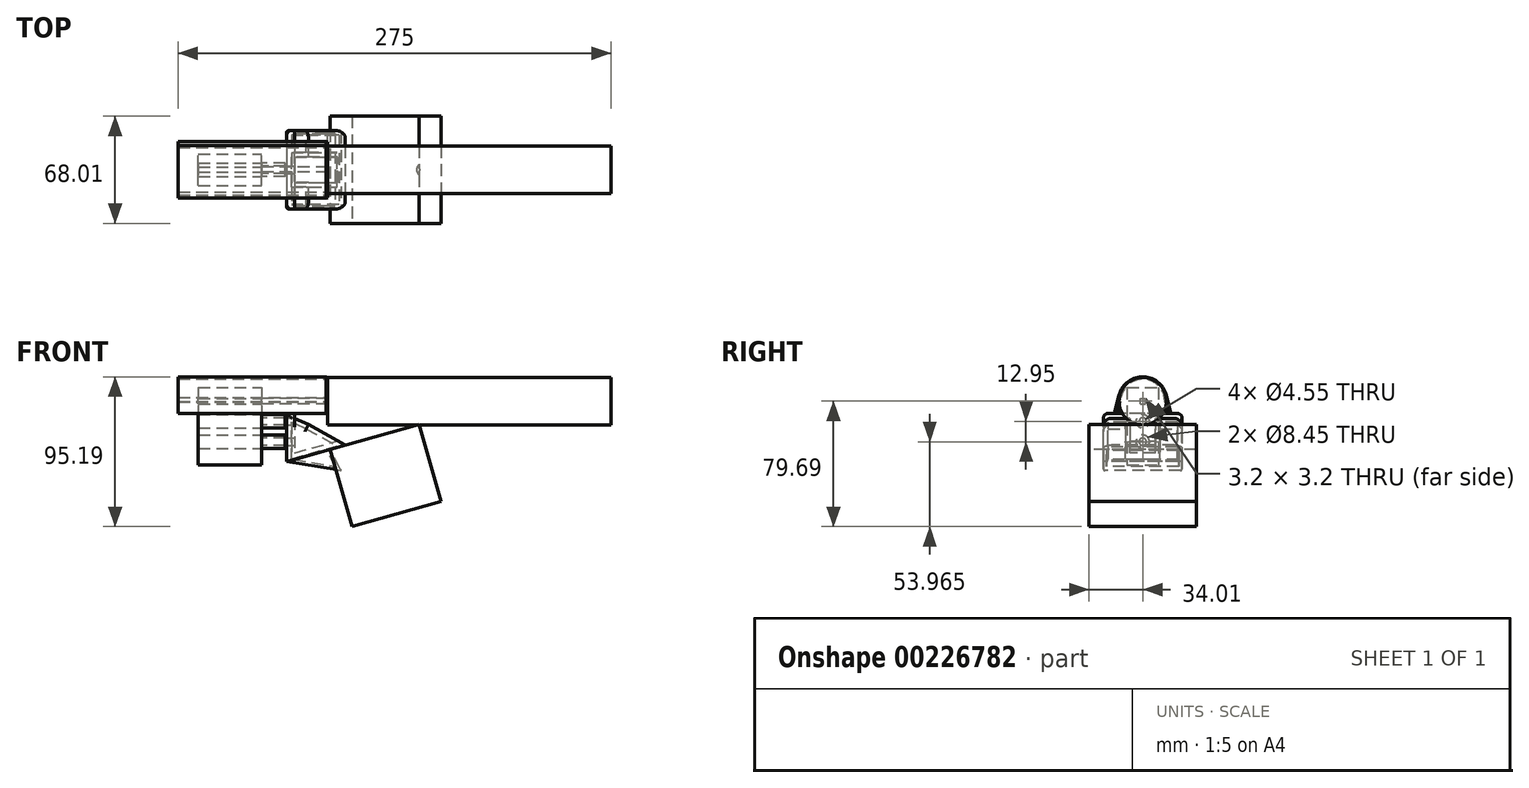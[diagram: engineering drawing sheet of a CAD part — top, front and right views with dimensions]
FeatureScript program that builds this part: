
annotation { "Feature Type Name" : "Feature", "Feature Type Description" : "" }
export const myFeature = defineFeature(function(context is Context, id is Id, definition is map)
    precondition{}
    {
        {
            var Q0;
            Q0=qCreatedBy(makeId("Right.planeOp"),FACE);
            var sketch = newSketch(context, id + "F0", { "sketchPlane" : qUnion([Q0])});
            skLineSegment(sketch, "E0.bottom", {"start": v(-20, 49.25) * mm, "end": v(0, 49.25) * mm});
            skLineSegment(sketch, "E0.top", {"start": v(-20, 0) * mm, "end": v(0, 0) * mm});
            skLineSegment(sketch, "E0.left", {"start": v(-20, 49.25) * mm, "end": v(-20, 0) * mm});
            skLineSegment(sketch, "E0.right", {"start": v(0, 49.25) * mm, "end": v(0, 0) * mm});
            skLineSegment(sketch, "E1.bottom", {"start": v(-11.6, 38.98) * mm, "end": v(-8.4, 38.98) * mm});
            skLineSegment(sketch, "E1.top", {"start": v(-11.6, 42.18) * mm, "end": v(-8.4, 42.18) * mm});
            skLineSegment(sketch, "E1.left", {"start": v(-11.6, 38.98) * mm, "end": v(-11.6, 42.18) * mm});
            skLineSegment(sketch, "E1.right", {"start": v(-8.4, 38.98) * mm, "end": v(-8.4, 42.18) * mm});
            skCircle(sketch, "E2", {"center": v(-10, 27.8) * mm, "radius": 4.22 * mm});
            skCircle(sketch, "E3", {"center": v(-10, 14.86) * mm, "radius": 4.22 * mm});
            skPoint(sketch, "E4", {"position": v(-10, 0) * mm});
            skPoint(sketch, "E5", {"position": v(-10, 38.98) * mm});
            skCircle(sketch, "E6", {"center": v(-10, 27.8) * mm, "radius": 2.27 * mm});
            skCircle(sketch, "E7", {"center": v(-10, 14.86) * mm, "radius": 2.27 * mm});
            skSolve(sketch);
        }
        {
            var Q0;
            Q0=makeQuery(id+"F0.imprint","IMPRINT",FACE,{"disambiguationData":[TD([[makeQuery(id+"F0.imprint","IMPRINT",EDGE,{"derivedFrom":sQuery(id+"F0.wireOp",EDGE,"E2")}),1.0]])]});
            var Q1;
            Q1=makeQuery(id+"F0.imprint","IMPRINT",FACE,{"disambiguationData":[TD([[makeQuery(id+"F0.imprint","IMPRINT",EDGE,{"derivedFrom":sQuery(id+"F0.wireOp",EDGE,"E3")}),1.0]])]});
            extrude(context, id + "F1", {"entities" : qUnion([Q0, Q1]), "depth" : 15 * mm});
        }
        {
            var Q0;
            Q0=makeQuery(id+"F0.imprint","IMPRINT",FACE,{"disambiguationData":[TD([[makeQuery(id+"F0.imprint","IMPRINT",EDGE,{"derivedFrom":sQuery(id+"F0.wireOp",EDGE,"E6")}),1.0]])]});
            var Q1;
            Q1=makeQuery(id+"F0.imprint","IMPRINT",FACE,{"disambiguationData":[TD([[makeQuery(id+"F0.imprint","IMPRINT",EDGE,{"derivedFrom":sQuery(id+"F0.wireOp",EDGE,"E7")}),1.0]])]});
            extrude(context, id + "F2", {"entities" : qUnion([Q0, Q1]), "depth" : 16.02 * mm});
        }
        {
            var Q0;
            Q0=makeQuery(id+"F0.imprint","IMPRINT",FACE,{"disambiguationData":[TD([[makeQuery(id+"F0.imprint","IMPRINT",EDGE,{"derivedFrom":sQuery(id+"F0.wireOp",EDGE,"E1.bottom")}),1.0]])]});
            extrude(context, id + "F3", {"entities" : qUnion([Q0]), "depth" : 42 * mm});
        }
        {
            var Q0;
            Q0=makeQuery(id+"F0.imprint","IMPRINT",FACE,{"disambiguationData":[TD([[makeQuery(id+"F0.imprint","IMPRINT",EDGE,{"derivedFrom":sQuery(id+"F0.wireOp",EDGE,"E0.bottom")}),-1.0]])]});
            extrude(context, id + "F4", {"entities" : qUnion([Q0]), "oppositeDirection" : true, "depth" : 40.2 * mm});
        }
        {
            var Q0;
            Q0=makeQuery(id+"F3.opExtrude","CAP_FACE",FACE,{"disambiguationData":[OSD([sQuery(id+"F0.wireOp",EDGE,"E1.bottom"),sQuery(id+"F0.wireOp",EDGE,"E1.top"),sQuery(id+"F0.wireOp",EDGE,"E1.left"),sQuery(id+"F0.wireOp",EDGE,"E1.right")])],"isStart":false});
            var sketch = newSketch(context, id + "F5", { "sketchPlane" : qUnion([Q0])});
            skCircle(sketch, "E8", {"center": v(-10, 40.58) * mm, "radius": 15 * mm});
            skSolve(sketch);
        }
        {
            var Q0;
            Q0=makeQuery(id+"F5.imprint","IMPRINT",FACE,{"disambiguationData":[TD([[makeQuery(id+"F5.imprint","IMPRINT",EDGE,{"derivedFrom":sQuery(id+"F5.wireOp",EDGE,"E8")}),1.0]])]});
            var Q1;
            Q1=makeQuery(id+"F5.imprint","IMPRINT",FACE,{"disambiguationData":[TD([[makeQuery(id+"F5.imprint","IMPRINT",EDGE,{"derivedFrom":makeQuery(id+"F3.opExtrude","CAP_EDGE",EDGE,{"disambiguationData":[OSD([sQuery(id+"F0.wireOp",EDGE,"E1.bottom")])],"isStart":false})}),1.0]])]});
            extrude(context, id + "F6", {"entities" : qUnion([Q0, Q1]), "depth" : 180 * mm});
        }
        {
            var Q0;
            Q0=makeQuery(id+"F1.opExtrude","CAP_FACE",FACE,{"disambiguationData":[OSD([sQuery(id+"F0.wireOp",EDGE,"E2"),sQuery(id+"F0.wireOp",EDGE,"E6")])],"isStart":false});
            var sketch = newSketch(context, id + "F7", { "sketchPlane" : qUnion([Q0])});
            skLineSegment(sketch, "E9.bottom", {"start": v(-35, 32.8) * mm, "end": v(15, 32.8) * mm});
            skLineSegment(sketch, "E9.top", {"start": v(-35, -2.2) * mm, "end": v(15, -2.2) * mm});
            skLineSegment(sketch, "E9.left", {"start": v(-35, 32.8) * mm, "end": v(-35, -2.2) * mm});
            skLineSegment(sketch, "E9.right", {"start": v(15, 32.8) * mm, "end": v(15, -2.2) * mm});
            skCircle(sketch, "E10", {"center": v(-10, 14.86) * mm, "radius": 4.22 * mm});
            skCircle(sketch, "E11", {"center": v(-10, 27.8) * mm, "radius": 4.22 * mm});
            skPoint(sketch, "E12", {"position": v(-10, 32.8) * mm});
            skCircle(sketch, "E13", {"center": v(-10, 27.8) * mm, "radius": 2.27 * mm});
            skCircle(sketch, "E14", {"center": v(-10, 14.86) * mm, "radius": 2.27 * mm});
            skSolve(sketch);
        }
        {
            var Q0;
            Q0=sQuery(id+"F7.wireOp",EDGE,"E9.top");
            var Q1;
            Q1=qCreatedBy(makeId("Right.planeOp"),FACE);
            cPlane(context, id + "F8", {"entities" : qUnion([Q0, Q1]), "cplaneType" : CPlaneType.LINE_ANGLE, "offset" : 25 * mm, "angle" : 105.8 * degree, "oppositeDirection" : true, "width" : 150 * mm, "height" : 150 * mm});
        }
        {
            var Q0;
            Q0=qCreatedBy(id+"F8.planeOp",FACE);
            cPlane(context, id + "F9", {"entities" : qUnion([Q0]), "cplaneType" : CPlaneType.OFFSET, "offset" : 3.93 * mm, "oppositeDirection" : true, "width" : 150 * mm, "height" : 150 * mm});
        }
        {
            var Q0;
            Q0=qCreatedBy(id+"F9.planeOp",FACE);
            var sketch = newSketch(context, id + "F10", { "sketchPlane" : qUnion([Q0])});
            skLineSegment(sketch, "E15.bottom", {"start": v(44.61, -24) * mm, "end": v(103.38, -24) * mm});
            skLineSegment(sketch, "E15.top", {"start": v(44.61, 44) * mm, "end": v(103.38, 44) * mm});
            skLineSegment(sketch, "E15.left", {"start": v(44.61, -24) * mm, "end": v(44.61, 44) * mm});
            skLineSegment(sketch, "E15.right", {"start": v(103.38, -24) * mm, "end": v(103.38, 44) * mm});
            skSolve(sketch);
        }
        {
            var Q0;
            Q0=makeQuery(id+"F10.imprint","IMPRINT",FACE,{"disambiguationData":[TD([[makeQuery(id+"F10.imprint","IMPRINT",EDGE,{"derivedFrom":sQuery(id+"F10.wireOp",EDGE,"E15.bottom")}),1.0]])]});
            extrude(context, id + "F11", {"entities" : qUnion([Q0]), "operationType" : NewBodyOperationType.ADD, "depth" : 51 * mm});
        }
        {
            var Q0;
            Q0=qCreatedBy(makeId("Front.planeOp"),FACE);
            cPlane(context, id + "F12", {"entities" : qUnion([Q0]), "cplaneType" : CPlaneType.OFFSET, "offset" : 35 * mm, "width" : 150 * mm, "height" : 150 * mm});
        }
        {
            var Q0;
            Q0=qCreatedBy(id+"F12.planeOp",FACE);
            var sketch = newSketch(context, id + "F13", { "sketchPlane" : qUnion([Q0])});
            skLineSegment(sketch, "E16", {"start": v(15, 32.8) * mm, "end": v(69.17, 32.8) * mm});
            skLineSegment(sketch, "E17", {"start": v(69.17, 32.8) * mm, "end": v(73.25, 18.37) * mm});
            skLineSegment(sketch, "E18", {"start": v(73.25, 18.37) * mm, "end": v(15, 1.89) * mm});
            skLineSegment(sketch, "E19", {"start": v(15, 1.89) * mm, "end": v(15, 32.8) * mm});
            skLineSegment(sketch, "E20", {"start": v(53.17, 12.69) * mm, "end": v(47.47, 32.8) * mm});
            skPoint(sketch, "E21", {"position": v(43.54, 9.96) * mm});
            skLineSegment(sketch, "E22", {"start": v(16, 2.17) * mm, "end": v(16, 32.8) * mm});
            skLineSegment(sketch, "E23", {"start": v(21, 32.8) * mm, "end": v(21, 7.74) * mm});
            skLineSegment(sketch, "E24", {"start": v(21, 7.74) * mm, "end": v(52.08, 16.54) * mm});
            skSolve(sketch);
        }
        {
            var Q0;
            {var subQ4=sQuery(id+"F13.wireOp",EDGE,"E22");Q0=makeQuery(id+"F13.imprint","IMPRINT",FACE,{"disambiguationData":[TD([[makeQuery(id+"F13.imprint","IMPRINT",EDGE,{"derivedFrom":subQ4}),-1.0]])]});}
            extrude(context, id + "F14", {"entities" : qUnion([Q0]), "oppositeDirection" : true, "depth" : 50 * mm});
        }
        {
            var Q0;
            Q0=makeQuery(id+"F14.opExtrude","SWEPT_FACE",FACE,{"disambiguationData":[OSD([sQuery(id+"F13.wireOp",EDGE,"E23")])]});
            var sketch = newSketch(context, id + "F15", { "sketchPlane" : qUnion([Q0])});
            skCircle(sketch, "E25", {"center": v(-10, 27.8) * mm, "radius": 2.27 * mm});
            skCircle(sketch, "E26", {"center": v(-10, 14.86) * mm, "radius": 2.27 * mm});
            skPoint(sketch, "E27", {"position": v(-10, 32.8) * mm});
            skPoint(sketch, "E28", {"position": v(-17, 7.74) * mm});
            skPoint(sketch, "E29", {"position": v(-3, 7.74) * mm});
            skLineSegment(sketch, "E30", {"start": v(-35, 7.74) * mm, "end": v(-17, 7.74) * mm});
            skLineSegment(sketch, "E31", {"start": v(15, 7.74) * mm, "end": v(-3, 7.74) * mm});
            skSolve(sketch);
        }
        {
            var Q0;
            Q0=makeQuery(id+"F15.imprint","IMPRINT",FACE,{"disambiguationData":[TD([[makeQuery(id+"F15.imprint","IMPRINT",EDGE,{"derivedFrom":sQuery(id+"F15.wireOp",EDGE,"E25")}),1.0]])]});
            var Q1;
            Q1=makeQuery(id+"F15.imprint","IMPRINT",FACE,{"disambiguationData":[TD([[makeQuery(id+"F15.imprint","IMPRINT",EDGE,{"derivedFrom":sQuery(id+"F15.wireOp",EDGE,"E26")}),1.0]])]});
            extrude(context, id + "F16", {"entities" : qUnion([Q0, Q1]), "operationType" : NewBodyOperationType.REMOVE, "oppositeDirection" : true, "depth" : 5 * mm});
        }
        {
            var Q0;
            Q0=makeQuery(id+"F14.opExtrude","CAP_FACE",FACE,{"disambiguationData":[OSD([sQuery(id+"F13.wireOp",EDGE,"E16"),sQuery(id+"F13.wireOp",EDGE,"E18"),sQuery(id+"F13.wireOp",EDGE,"E20"),sQuery(id+"F13.wireOp",EDGE,"E22"),sQuery(id+"F13.wireOp",EDGE,"E23"),sQuery(id+"F13.wireOp",EDGE,"E24")])],"isStart":true});
            var sketch = newSketch(context, id + "F17", { "sketchPlane" : qUnion([Q0])});
            skLineSegment(sketch, "E32", {"start": v(21, 29.74) * mm, "end": v(50.87, 16.2) * mm});
            skLineSegment(sketch, "E33", {"start": v(50.87, 16.2) * mm, "end": v(21, 7.74) * mm});
            skLineSegment(sketch, "E34", {"start": v(21, 7.74) * mm, "end": v(21, 29.74) * mm});
            skSolve(sketch);
        }
        {
            var Q0;
            Q0=makeQuery(id+"F17.imprint","IMPRINT",FACE,{"disambiguationData":[TD([[makeQuery(id+"F17.imprint","IMPRINT",EDGE,{"derivedFrom":sQuery(id+"F17.wireOp",EDGE,"E32")}),-1.0]])]});
            extrude(context, id + "F18", {"entities" : qUnion([Q0]), "operationType" : NewBodyOperationType.ADD, "oppositeDirection" : true, "depth" : 50 * mm});
        }
        {
            var Q0;
            Q0=qCreatedBy(id+"F12.planeOp",FACE);
            cPlane(context, id + "F19", {"entities" : qUnion([Q0]), "cplaneType" : CPlaneType.OFFSET, "offset" : 17 * mm, "oppositeDirection" : true, "width" : 150 * mm, "height" : 150 * mm});
        }
        {
            var Q0;
            Q0=qCreatedBy(id+"F19.planeOp",FACE);
            var sketch = newSketch(context, id + "F20", { "sketchPlane" : qUnion([Q0])});
            skLineSegment(sketch, "E35", {"start": v(21, 29.74) * mm, "end": v(21, 7.74) * mm});
            skLineSegment(sketch, "E36", {"start": v(21, 7.74) * mm, "end": v(50.87, 16.2) * mm});
            skLineSegment(sketch, "E37", {"start": v(50.87, 16.2) * mm, "end": v(21, 29.74) * mm});
            skSolve(sketch);
        }
        {
            var Q0;
            Q0=makeQuery(id+"F20.imprint","IMPRINT",FACE,{"disambiguationData":[TD([[makeQuery(id+"F20.imprint","IMPRINT",EDGE,{"derivedFrom":sQuery(id+"F20.wireOp",EDGE,"E35")}),1.0]])]});
            extrude(context, id + "F21", {"entities" : qUnion([Q0]), "operationType" : NewBodyOperationType.REMOVE, "oppositeDirection" : true, "depth" : 16 * mm});
        }
        {
            var Q0;
            Q0=makeQuery(id+"F14.opExtrude","SWEPT_EDGE",EDGE,{"disambiguationData":[OSD([sQuery(id+"F13.wireOp",EDGE,"E20"),sQuery(id+"F13.wireOp",EDGE,"E24")])]});
            chamfer(context, id + "F22", {"entities" : qUnion([Q0]), "width" : 4 * mm, "tangentPropagation" : true});
        }
        {
            var Q0;
            {var subQ2=sQuery(id+"F17.wireOp",EDGE,"E33");Q0=makeQuery(id+"F17.imprint","IMPRINT",FACE,{"disambiguationData":[TD([[makeQuery(id+"F17.imprint","IMPRINT",EDGE,{"derivedFrom":subQ2}),-1.0]])]});}
            var sketch = newSketch(context, id + "F23", { "sketchPlane" : qUnion([Q0])});
            skLineSegment(sketch, "E38", {"start": v(16, 2.17) * mm, "end": v(50.33, -3.41) * mm});
            skLineSegment(sketch, "E39", {"start": v(50.33, -3.41) * mm, "end": v(43.54, 9.96) * mm});
            skLineSegment(sketch, "E40", {"start": v(43.54, 9.96) * mm, "end": v(16, 2.17) * mm});
            skSolve(sketch);
        }
        {
            var Q0;
            Q0=makeQuery(id+"F23.imprint","IMPRINT",FACE,{"disambiguationData":[TD([[makeQuery(id+"F23.imprint","IMPRINT",EDGE,{"derivedFrom":sQuery(id+"F23.wireOp",EDGE,"E38")}),1.0]])]});
            extrude(context, id + "F24", {"entities" : qUnion([Q0]), "oppositeDirection" : true, "depth" : 50 * mm});
        }
        {
            var Q0;
            Q0=makeQuery(id+"F24.opExtrude","SWEPT_FACE",FACE,{"disambiguationData":[OSD([sQuery(id+"F23.wireOp",EDGE,"E40")])]});
            shell(context, id + "F25", {"entities" : qUnion([Q0]), "thickness" : 2 * mm});
        }
        {
            var Q0;
            Q0=makeQuery(id+"F3.opExtrude","CAP_FACE",FACE,{"disambiguationData":[OSD([sQuery(id+"F0.wireOp",EDGE,"E1.bottom"),sQuery(id+"F0.wireOp",EDGE,"E1.top"),sQuery(id+"F0.wireOp",EDGE,"E1.left"),sQuery(id+"F0.wireOp",EDGE,"E1.right")])],"isStart":false});
            var sketch = newSketch(context, id + "F26", { "sketchPlane" : qUnion([Q0])});
            skCircle(sketch, "E41", {"center": v(-10, 40.58) * mm, "radius": 14 * mm});
            skLineSegment(sketch, "E42", {"start": v(-11.6, 42.18) * mm, "end": v(-8.4, 38.98) * mm, "construction": true});
            skLineSegment(sketch, "E43", {"start": v(-11.6, 38.98) * mm, "end": v(-8.4, 42.18) * mm, "construction": true});
            skCircle(sketch, "E44", {"center": v(-10, 40.58) * mm, "radius": 15.5 * mm});
            skLineSegment(sketch, "E45", {"start": v(-29.96, 32.8) * mm, "end": v(12, 32.8) * mm});
            skLineSegment(sketch, "E46", {"start": v(-25, 44.52) * mm, "end": v(-28.07, 32.8) * mm});
            skLineSegment(sketch, "E47", {"start": v(5.31, 42.98) * mm, "end": v(8.07, 32.8) * mm});
            skLineSegment(sketch, "E48", {"start": v(-24, 40.42) * mm, "end": v(-26, 32.8) * mm});
            skLineSegment(sketch, "E49", {"start": v(4, 40.2) * mm, "end": v(6, 32.8) * mm});
            skSolve(sketch);
        }
        {
            var Q0;
            {var subQ2=sQuery(id+"F26.wireOp",EDGE,"E48");var subQ7=sQuery(id+"F26.wireOp",EDGE,"E41");var subQ8=makeQuery(id+"F26.imprint","INTERSECT",VERTEX,{"derivedFrom":[subQ7,subQ2]});Q0=makeQuery(id+"F26.imprint","IMPRINT",FACE,{"disambiguationData":[TD([[makeQuery(id+"F26.imprint","IMPRINT",EDGE,{"disambiguationData":[TD([[subQ8,1.0]])],"derivedFrom":subQ7}),-1.0]])]});}
            var Q1;
            {var subQ0=sQuery(id+"F26.wireOp",EDGE,"E46");Q1=makeQuery(id+"F26.imprint","IMPRINT",FACE,{"disambiguationData":[TD([[makeQuery(id+"F26.imprint","IMPRINT",EDGE,{"derivedFrom":subQ0}),1.0]])]});}
            var Q2;
            {var subQ0=sQuery(id+"F26.wireOp",EDGE,"E47");Q2=makeQuery(id+"F26.imprint","IMPRINT",FACE,{"disambiguationData":[TD([[makeQuery(id+"F26.imprint","IMPRINT",EDGE,{"derivedFrom":subQ0}),-1.0]])]});}
            extrude(context, id + "F27", {"entities" : qUnion([Q0, Q1, Q2]), "oppositeDirection" : true, "depth" : 95 * mm});
        }
        {
            var Q0;
            Q0=makeQuery(id+"F27.opExtrude","CAP_EDGE",EDGE,{"disambiguationData":[OSD([sQuery(id+"F26.wireOp",EDGE,"E44")])],"isStart":true});
            var Q1;
            Q1=makeQuery(id+"F27.opExtrude","CAP_EDGE",EDGE,{"disambiguationData":[OSD([sQuery(id+"F26.wireOp",EDGE,"E46")])],"isStart":true});
            var Q2;
            Q2=makeQuery(id+"F27.opExtrude","CAP_EDGE",EDGE,{"disambiguationData":[OSD([sQuery(id+"F26.wireOp",EDGE,"E47")])],"isStart":true});
            chamfer(context, id + "F28", {"entities" : qUnion([Q0, Q1, Q2]), "chamferType" : ChamferType.TWO_OFFSETS, "width1" : .5 * mm, "oppositeDirection" : false, "width2" : 1 * mm, "tangentPropagation" : true});
        }
        {
            var Q0;
            Q0=makeQuery(id+"F14.opExtrude","SWEPT_FACE",FACE,{"disambiguationData":[OSD([sQuery(id+"F13.wireOp",EDGE,"E18")])]});
            shell(context, id + "F29", {"entities" : qUnion([Q0]), "thickness" : 3 * mm});
        }
        {
            var Q0;
            {var subQ0=sQuery(id+"F13.wireOp",EDGE,"E24");var subQ1=sQuery(id+"F13.wireOp",EDGE,"E20");Q0=makeQuery(id+"F22.opChamfer","BLEND_EDGE",EDGE,{"blendedFrom":[makeQuery(id+"F14.opExtrude","SWEPT_EDGE",EDGE,{"disambiguationData":[OSD([subQ1,subQ0])]}),makeQuery(id+"F18.boolean.opBoolean","MERGE",FACE,{"derivedFrom":[makeQuery(id+"F14.opExtrude","CAP_FACE",FACE,{"disambiguationData":[OSD([sQuery(id+"F13.wireOp",EDGE,"E16"),sQuery(id+"F13.wireOp",EDGE,"E18"),subQ1,sQuery(id+"F13.wireOp",EDGE,"E22"),sQuery(id+"F13.wireOp",EDGE,"E23"),subQ0])],"isStart":false}),makeQuery(id+"F18.opExtrude","CAP_FACE",FACE,{"disambiguationData":[OSD([sQuery(id+"F17.wireOp",EDGE,"E32"),sQuery(id+"F17.wireOp",EDGE,"E33"),sQuery(id+"F17.wireOp",EDGE,"E34")])],"isStart":false})]})],"blendedInto":[makeQuery(id+"F18.boolean.opBoolean","MERGE",FACE,{"derivedFrom":[makeQuery(id+"F14.opExtrude","CAP_FACE",FACE,{"disambiguationData":[OSD([sQuery(id+"F13.wireOp",EDGE,"E16"),sQuery(id+"F13.wireOp",EDGE,"E18"),subQ1,sQuery(id+"F13.wireOp",EDGE,"E22"),sQuery(id+"F13.wireOp",EDGE,"E23"),subQ0])],"isStart":false}),makeQuery(id+"F18.opExtrude","CAP_FACE",FACE,{"disambiguationData":[OSD([sQuery(id+"F17.wireOp",EDGE,"E32"),sQuery(id+"F17.wireOp",EDGE,"E33"),sQuery(id+"F17.wireOp",EDGE,"E34")])],"isStart":false})]})]});}
            var Q1;
            {var subQ0=sQuery(id+"F13.wireOp",EDGE,"E24");var subQ1=sQuery(id+"F13.wireOp",EDGE,"E20");Q1=makeQuery(id+"F22.opChamfer","BLEND_EDGE",EDGE,{"blendedFrom":[makeQuery(id+"F14.opExtrude","SWEPT_EDGE",EDGE,{"disambiguationData":[OSD([subQ1,subQ0])]}),makeQuery(id+"F18.boolean.opBoolean","MERGE",FACE,{"derivedFrom":[makeQuery(id+"F14.opExtrude","CAP_FACE",FACE,{"disambiguationData":[OSD([sQuery(id+"F13.wireOp",EDGE,"E16"),sQuery(id+"F13.wireOp",EDGE,"E18"),subQ1,sQuery(id+"F13.wireOp",EDGE,"E22"),sQuery(id+"F13.wireOp",EDGE,"E23"),subQ0])],"isStart":true}),makeQuery(id+"F18.opExtrude","CAP_FACE",FACE,{"disambiguationData":[OSD([sQuery(id+"F17.wireOp",EDGE,"E32"),sQuery(id+"F17.wireOp",EDGE,"E33"),sQuery(id+"F17.wireOp",EDGE,"E34")])],"isStart":true})]})],"blendedInto":[makeQuery(id+"F18.boolean.opBoolean","MERGE",FACE,{"derivedFrom":[makeQuery(id+"F14.opExtrude","CAP_FACE",FACE,{"disambiguationData":[OSD([sQuery(id+"F13.wireOp",EDGE,"E16"),sQuery(id+"F13.wireOp",EDGE,"E18"),subQ1,sQuery(id+"F13.wireOp",EDGE,"E22"),sQuery(id+"F13.wireOp",EDGE,"E23"),subQ0])],"isStart":true}),makeQuery(id+"F18.opExtrude","CAP_FACE",FACE,{"disambiguationData":[OSD([sQuery(id+"F17.wireOp",EDGE,"E32"),sQuery(id+"F17.wireOp",EDGE,"E33"),sQuery(id+"F17.wireOp",EDGE,"E34")])],"isStart":true})]})]});}
            var Q2;
            Q2=makeQuery(id+"F18.opExtrude","CAP_EDGE",EDGE,{"disambiguationData":[OSD([sQuery(id+"F17.wireOp",EDGE,"E32")])],"isStart":true});
            var Q3;
            Q3=makeQuery(id+"F18.opExtrude","CAP_EDGE",EDGE,{"disambiguationData":[OSD([sQuery(id+"F17.wireOp",EDGE,"E32")])],"isStart":false});
            fillet(context, id + "F30", {"entities" : qUnion([Q0, Q1, Q2, Q3]), "radius" : 5 * mm, "tangentPropagation" : true, "allowEdgeOverflow" : false});
        }
        {
            var Q0;
            Q0=makeQuery(id+"F14.opExtrude","CAP_EDGE",EDGE,{"disambiguationData":[OSD([sQuery(id+"F13.wireOp",EDGE,"E16")])],"isStart":true});
            var Q1;
            Q1=makeQuery(id+"F14.opExtrude","CAP_EDGE",EDGE,{"disambiguationData":[OSD([sQuery(id+"F13.wireOp",EDGE,"E22")])],"isStart":true});
            var Q2;
            Q2=makeQuery(id+"F14.opExtrude","CAP_EDGE",EDGE,{"disambiguationData":[OSD([sQuery(id+"F13.wireOp",EDGE,"E16")])],"isStart":false});
            var Q3;
            Q3=makeQuery(id+"F14.opExtrude","CAP_EDGE",EDGE,{"disambiguationData":[OSD([sQuery(id+"F13.wireOp",EDGE,"E22")])],"isStart":false});
            fillet(context, id + "F31", {"entities" : qUnion([Q0, Q1, Q2, Q3]), "radius" : 3 * mm, "tangentPropagation" : true, "allowEdgeOverflow" : false});
        }
        {
            var Q0;
            Q0=makeQuery(id+"F24.opExtrude","CAP_EDGE",EDGE,{"disambiguationData":[OSD([sQuery(id+"F23.wireOp",EDGE,"E38")])],"isStart":false});
            var Q1;
            Q1=makeQuery(id+"F24.opExtrude","CAP_EDGE",EDGE,{"disambiguationData":[OSD([sQuery(id+"F23.wireOp",EDGE,"E38")])],"isStart":true});
            fillet(context, id + "F32", {"entities" : qUnion([Q0, Q1]), "radius" : 1 * mm, "tangentPropagation" : true, "allowEdgeOverflow" : false});
        }
    });
